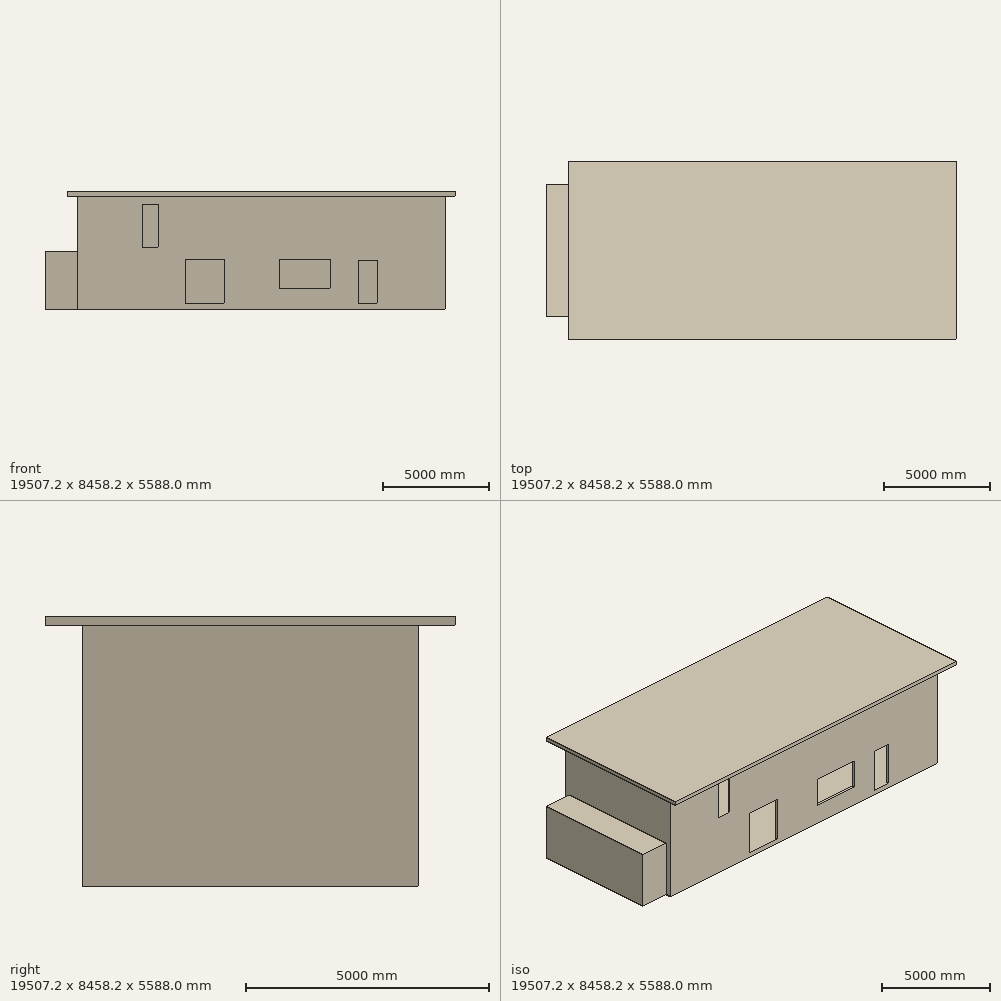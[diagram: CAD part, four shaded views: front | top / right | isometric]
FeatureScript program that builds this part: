
annotation { "Feature Type Name" : "Feature", "Feature Type Description" : "" }
export const myFeature = defineFeature(function(context is Context, id is Id, definition is map)
    precondition{}
    {
        {
            var Q0;
            Q0=qCreatedBy(makeId("Front.planeOp"),FACE);
            var sketch = newSketch(context, id + "F0", { "sketchPlane" : qUnion([Q0])});
            skLineSegment(sketch, "E0.bottom", {"start": v(0, 0) * mm, "end": v(17526, 0) * mm});
            skLineSegment(sketch, "E0.top", {"start": v(0, 5384.8) * mm, "end": v(17526, 5384.8) * mm});
            skLineSegment(sketch, "E0.left", {"start": v(0, 0) * mm, "end": v(0, 5384.8) * mm});
            skLineSegment(sketch, "E0.right", {"start": v(17526, 0) * mm, "end": v(17526, 5384.8) * mm});
            skSolve(sketch);
        }
        {
            var Q0;
            Q0=makeQuery(id+"F0.imprint","IMPRINT",FACE,{"disambiguationData":[TD([[makeQuery(id+"F0.imprint","IMPRINT",EDGE,{"derivedFrom":sQuery(id+"F0.wireOp",EDGE,"E0.bottom")}),1.0]])]});
            extrude(context, id + "F1", {"entities" : qUnion([Q0]), "depth" : 6934.2 * mm});
        }
        {
            var Q0;
            Q0=makeQuery(id+"F1.opExtrude","SWEPT_FACE",FACE,{"disambiguationData":[OSD([sQuery(id+"F0.wireOp",EDGE,"E0.top")])]});
            shell(context, id + "F2", {"entities" : qUnion([Q0]), "thickness" : 254 * mm});
        }
        {
            var Q0;
            Q0=makeQuery(id+"F1.opExtrude","SWEPT_FACE",FACE,{"disambiguationData":[OSD([sQuery(id+"F0.wireOp",EDGE,"E0.top")])]});
            var sketch = newSketch(context, id + "F3", { "sketchPlane" : qUnion([Q0])});
            skLineSegment(sketch, "E1.bottom", {"start": v(114.3, -114.3) * mm, "end": v(17411.7, -114.3) * mm});
            skLineSegment(sketch, "E1.top", {"start": v(114.3, -6819.9) * mm, "end": v(17411.7, -6819.9) * mm});
            skLineSegment(sketch, "E1.left", {"start": v(114.3, -114.3) * mm, "end": v(114.3, -6819.9) * mm});
            skLineSegment(sketch, "E1.right", {"start": v(17411.7, -114.3) * mm, "end": v(17411.7, -6819.9) * mm});
            skLineSegment(sketch, "E2", {"start": v(8763, -114.3) * mm, "end": v(8763, -6819.9) * mm, "construction": true});
            skLineSegment(sketch, "E3", {"start": v(17411.7, -3467.1) * mm, "end": v(114.3, -3467.1) * mm, "construction": true});
            skSolve(sketch);
        }
        {
            var Q0;
            Q0=makeQuery(id+"F3.imprint","IMPRINT",FACE,{"disambiguationData":[TD([[makeQuery(id+"F3.imprint","IMPRINT",EDGE,{"derivedFrom":sQuery(id+"F3.wireOp",EDGE,"E1.bottom")}),-1.0]])]});
            extrude(context, id + "F4", {"entities" : qUnion([Q0]), "operationType" : NewBodyOperationType.REMOVE, "oppositeDirection" : true, "depth" : 5130.8 * mm});
        }
        {
            var Q0;
            Q0=makeQuery(id+"F1.opExtrude","CAP_FACE",FACE,{"disambiguationData":[OSD([sQuery(id+"F0.wireOp",EDGE,"E0.bottom"),sQuery(id+"F0.wireOp",EDGE,"E0.top"),sQuery(id+"F0.wireOp",EDGE,"E0.left"),sQuery(id+"F0.wireOp",EDGE,"E0.right")])],"isStart":false});
            var sketch = newSketch(context, id + "F5", { "sketchPlane" : qUnion([Q0])});
            skLineSegment(sketch, "E4.bottom", {"start": v(5486.4, 2367.28) * mm, "end": v(7924.8, 2367.28) * mm});
            skLineSegment(sketch, "E4.top", {"start": v(5486.4, 965.2) * mm, "end": v(7924.8, 965.2) * mm});
            skLineSegment(sketch, "E4.left", {"start": v(5486.4, 2367.28) * mm, "end": v(5486.4, 965.2) * mm});
            skLineSegment(sketch, "E4.right", {"start": v(7924.8, 2367.28) * mm, "end": v(7924.8, 965.2) * mm});
            skSolve(sketch);
        }
        {
            var Q0;
            Q0=makeQuery(id+"F1.opExtrude","CAP_FACE",FACE,{"disambiguationData":[OSD([sQuery(id+"F0.wireOp",EDGE,"E0.bottom"),sQuery(id+"F0.wireOp",EDGE,"E0.top"),sQuery(id+"F0.wireOp",EDGE,"E0.left"),sQuery(id+"F0.wireOp",EDGE,"E0.right")])],"isStart":false});
            var sketch = newSketch(context, id + "F6", { "sketchPlane" : qUnion([Q0])});
            skLineSegment(sketch, "E5.bottom", {"start": v(9601.2, 2367.28) * mm, "end": v(12039.6, 2367.28) * mm});
            skLineSegment(sketch, "E5.top", {"start": v(9601.2, 965.2) * mm, "end": v(12039.6, 965.2) * mm});
            skLineSegment(sketch, "E5.left", {"start": v(9601.2, 2367.28) * mm, "end": v(9601.2, 965.2) * mm});
            skLineSegment(sketch, "E5.right", {"start": v(12039.6, 2367.28) * mm, "end": v(12039.6, 965.2) * mm});
            skLineSegment(sketch, "E6", {"start": v(8763, 5384.8) * mm, "end": v(8763, 0) * mm, "construction": true});
            skSolve(sketch);
        }
        {
            var Q0;
            Q0 = qSketchRegion(id + "F6", true);
            extrude(context, id + "F7", {"entities" : qUnion([Q0]), "operationType" : NewBodyOperationType.REMOVE, "endBound" : BoundingType.UP_TO_NEXT, "oppositeDirection" : true, "depth" : 25.4 * mm});
        }
        {
            var Q0;
            Q0=makeQuery(id+"F2.opShell","OFFSET_FACE",FACE,{"disambiguationData":[OSD([sQuery(id+"F0.wireOp",EDGE,"E0.bottom")])]});
            var sketch = newSketch(context, id + "F8", { "sketchPlane" : qUnion([Q0])});
            skLineSegment(sketch, "E7.bottom", {"start": v(4737.1, -6819.9) * mm, "end": v(1498.6, -6819.9) * mm, "construction": true});
            skLineSegment(sketch, "E7.top", {"start": v(4737.1, -5689.6) * mm, "end": v(1498.6, -5689.6) * mm});
            skLineSegment(sketch, "E7.left", {"start": v(4737.1, -6819.9) * mm, "end": v(4737.1, -5689.6) * mm});
            skLineSegment(sketch, "E7.right", {"start": v(1498.6, -6819.9) * mm, "end": v(1498.6, -5689.6) * mm});
            skLineSegment(sketch, "E8", {"start": v(1498.6, -6819.9) * mm, "end": v(1384.3, -6819.9) * mm});
            skLineSegment(sketch, "E9", {"start": v(1384.3, -6819.9) * mm, "end": v(1384.3, -5575.3) * mm});
            skLineSegment(sketch, "E10", {"start": v(1384.3, -5575.3) * mm, "end": v(4851.4, -5575.3) * mm});
            skLineSegment(sketch, "E11", {"start": v(4851.4, -5575.3) * mm, "end": v(4851.4, -6819.9) * mm});
            skLineSegment(sketch, "E12", {"start": v(4851.4, -6819.9) * mm, "end": v(4737.1, -6819.9) * mm});
            skSolve(sketch);
        }
        {
            var Q0;
            Q0 = qSketchRegion(id + "F8", true);
            extrude(context, id + "F9", {"entities" : qUnion([Q0]), "operationType" : NewBodyOperationType.ADD, "depth" : 2438.4 * mm});
        }
        {
            var Q0;
            Q0=makeQuery(id+"F1.opExtrude","SWEPT_FACE",FACE,{"disambiguationData":[OSD([sQuery(id+"F0.wireOp",EDGE,"E0.top")])]});
            var sketch = newSketch(context, id + "F10", { "sketchPlane" : qUnion([Q0])});
            skLineSegment(sketch, "E13.bottom", {"start": v(-457.2, -7696.2) * mm, "end": v(17983.2, -7696.2) * mm});
            skLineSegment(sketch, "E13.top", {"start": v(-457.2, 762) * mm, "end": v(17983.2, 762) * mm});
            skLineSegment(sketch, "E13.left", {"start": v(-457.2, -7696.2) * mm, "end": v(-457.2, 762) * mm});
            skLineSegment(sketch, "E13.right", {"start": v(17983.2, -7696.2) * mm, "end": v(17983.2, 762) * mm});
            skLineSegment(sketch, "E14", {"start": v(8763, -6819.9) * mm, "end": v(8763, -114.3) * mm, "construction": true});
            skLineSegment(sketch, "E15", {"start": v(114.3, -3467.1) * mm, "end": v(17411.7, -3467.1) * mm, "construction": true});
            skSolve(sketch);
        }
        {
            var Q0;
            Q0 = qSketchRegion(id + "F10", true);
            extrude(context, id + "F11", {"entities" : qUnion([Q0]), "depth" : 203.2 * mm});
        }
        {
            var Q0;
            Q0=makeQuery(id+"F9.opExtrude","CAP_FACE",FACE,{"disambiguationData":[OSD([sQuery(id+"F8.wireOp",EDGE,"E7.top"),sQuery(id+"F8.wireOp",EDGE,"E7.left"),sQuery(id+"F8.wireOp",EDGE,"E7.right"),sQuery(id+"F8.wireOp",EDGE,"E8"),sQuery(id+"F8.wireOp",EDGE,"E9"),sQuery(id+"F8.wireOp",EDGE,"E10"),sQuery(id+"F8.wireOp",EDGE,"E11"),sQuery(id+"F8.wireOp",EDGE,"E12")])],"isStart":false});
            var sketch = newSketch(context, id + "F12", { "sketchPlane" : qUnion([Q0])});
            skLineSegment(sketch, "E16.bottom", {"start": v(114.3, -6819.9) * mm, "end": v(17411.7, -6819.9) * mm});
            skLineSegment(sketch, "E16.top", {"start": v(114.3, -114.3) * mm, "end": v(17411.7, -114.3) * mm});
            skLineSegment(sketch, "E16.left", {"start": v(114.3, -6819.9) * mm, "end": v(114.3, -114.3) * mm});
            skLineSegment(sketch, "E16.right", {"start": v(17411.7, -6819.9) * mm, "end": v(17411.7, -114.3) * mm});
            skSolve(sketch);
        }
        {
            var Q0;
            Q0 = qSketchRegion(id + "F12", true);
            extrude(context, id + "F13", {"entities" : qUnion([Q0]), "operationType" : NewBodyOperationType.ADD, "depth" : 254 * mm});
        }
        {
            var Q0;
            Q0=makeQuery(id+"F1.opExtrude","CAP_FACE",FACE,{"disambiguationData":[OSD([sQuery(id+"F0.wireOp",EDGE,"E0.bottom"),sQuery(id+"F0.wireOp",EDGE,"E0.top"),sQuery(id+"F0.wireOp",EDGE,"E0.left"),sQuery(id+"F0.wireOp",EDGE,"E0.right")])],"isStart":false});
            var sketch = newSketch(context, id + "F14", { "sketchPlane" : qUnion([Q0])});
            skLineSegment(sketch, "E17.bottom", {"start": v(13360.4, 2336.8) * mm, "end": v(14274.8, 2336.8) * mm});
            skLineSegment(sketch, "E17.top", {"start": v(13360.4, 254) * mm, "end": v(14274.8, 254) * mm});
            skLineSegment(sketch, "E17.left", {"start": v(13360.4, 2336.8) * mm, "end": v(13360.4, 254) * mm});
            skLineSegment(sketch, "E17.right", {"start": v(14274.8, 2336.8) * mm, "end": v(14274.8, 254) * mm});
            skSolve(sketch);
        }
        {
            var Q0;
            Q0 = qSketchRegion(id + "F14", true);
            extrude(context, id + "F15", {"entities" : qUnion([Q0]), "operationType" : NewBodyOperationType.REMOVE, "endBound" : BoundingType.UP_TO_NEXT, "oppositeDirection" : true, "depth" : 25.4 * mm});
        }
        {
            var Q0;
            Q0=qCreatedBy(makeId("Top.planeOp"),FACE);
            var sketch = newSketch(context, id + "F16", { "sketchPlane" : qUnion([Q0])});
            skLineSegment(sketch, "E18.bottom", {"start": v(0, -304.8) * mm, "end": v(-1524, -304.8) * mm});
            skLineSegment(sketch, "E18.top", {"start": v(0, -6629.4) * mm, "end": v(-1524, -6629.4) * mm});
            skLineSegment(sketch, "E18.left", {"start": v(0, -304.8) * mm, "end": v(0, -6629.4) * mm});
            skLineSegment(sketch, "E18.right", {"start": v(-1524, -304.8) * mm, "end": v(-1524, -6629.4) * mm});
            skSolve(sketch);
        }
        {
            var Q0;
            Q0 = qSketchRegion(id + "F16", true);
            extrude(context, id + "F17", {"entities" : qUnion([Q0]), "operationType" : NewBodyOperationType.ADD, "depth" : 2743.2 * mm});
        }
        {
            var Q0;
            Q0=makeQuery(id+"F1.opExtrude","CAP_FACE",FACE,{"disambiguationData":[OSD([sQuery(id+"F0.wireOp",EDGE,"E0.bottom"),sQuery(id+"F0.wireOp",EDGE,"E0.top"),sQuery(id+"F0.wireOp",EDGE,"E0.left"),sQuery(id+"F0.wireOp",EDGE,"E0.right")])],"isStart":false});
            var sketch = newSketch(context, id + "F18", { "sketchPlane" : qUnion([Q0])});
            skLineSegment(sketch, "E19.bottom", {"start": v(5156.2, 2367.28) * mm, "end": v(6985, 2367.28) * mm});
            skLineSegment(sketch, "E19.top", {"start": v(5156.2, 254) * mm, "end": v(6985, 254) * mm});
            skLineSegment(sketch, "E19.left", {"start": v(5156.2, 2367.28) * mm, "end": v(5156.2, 254) * mm});
            skLineSegment(sketch, "E19.right", {"start": v(6985, 2367.28) * mm, "end": v(6985, 254) * mm});
            skSolve(sketch);
        }
        {
            var Q0;
            Q0 = qSketchRegion(id + "F18", true);
            extrude(context, id + "F19", {"entities" : qUnion([Q0]), "operationType" : NewBodyOperationType.REMOVE, "endBound" : BoundingType.UP_TO_NEXT, "oppositeDirection" : true, "depth" : 25.4 * mm});
        }
        {
            var Q0;
            Q0=makeQuery(id+"F1.opExtrude","CAP_FACE",FACE,{"disambiguationData":[OSD([sQuery(id+"F0.wireOp",EDGE,"E0.bottom"),sQuery(id+"F0.wireOp",EDGE,"E0.top"),sQuery(id+"F0.wireOp",EDGE,"E0.left"),sQuery(id+"F0.wireOp",EDGE,"E0.right")])],"isStart":false});
            var sketch = newSketch(context, id + "F20", { "sketchPlane" : qUnion([Q0])});
            skLineSegment(sketch, "E20.bottom", {"start": v(3111.5, 4978.4) * mm, "end": v(3873.5, 4978.4) * mm});
            skLineSegment(sketch, "E20.top", {"start": v(3111.5, 2946.4) * mm, "end": v(3873.5, 2946.4) * mm});
            skLineSegment(sketch, "E20.left", {"start": v(3111.5, 4978.4) * mm, "end": v(3111.5, 2946.4) * mm});
            skLineSegment(sketch, "E20.right", {"start": v(3873.5, 4978.4) * mm, "end": v(3873.5, 2946.4) * mm});
            skSolve(sketch);
        }
        {
            var Q0;
            Q0 = qSketchRegion(id + "F20", true);
            extrude(context, id + "F21", {"entities" : qUnion([Q0]), "operationType" : NewBodyOperationType.REMOVE, "endBound" : BoundingType.UP_TO_NEXT, "oppositeDirection" : true, "depth" : 25.4 * mm});
        }
    });
